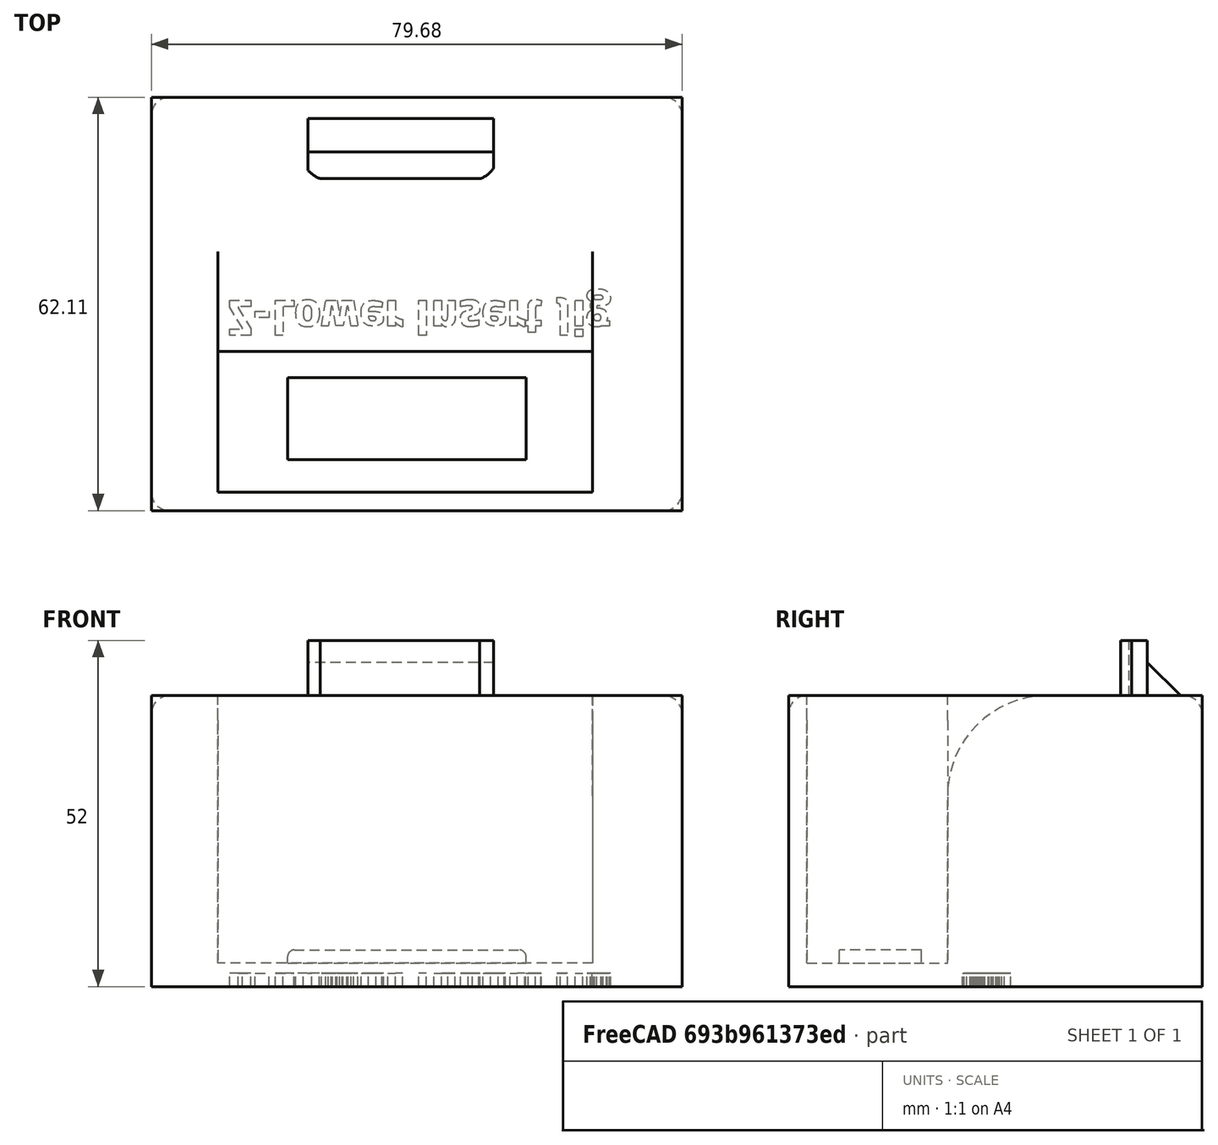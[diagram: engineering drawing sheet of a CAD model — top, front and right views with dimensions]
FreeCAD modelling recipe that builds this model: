
FCSTD DOCUMENT  (FreeCAD 0.17R9643 (Git))
Label: Z_lower_left_insert_jig
License: All rights reserved
LicenseURL: http://en.wikipedia.org/wiki/All_rights_reserved
objects: Sketcher::SketchObject×4, PartDesign::Pad×4, PartDesign::Fillet×3, PartDesign::Body×3, PartDesign::Pocket×2, PartDesign::Plane×2, Mesh::Feature×1, Part::Feature×1, PartDesign::Chamfer×1, Part::Part2DObjectPython×1, App::Part×1
note: 27 computed .brp shape members not serialized (recipe doc carries the construction recipe); baked Part::Feature solids carry a one-line shape summary decoded from their .brp

FEATURE [Sketcher::SketchObject] Sketch
  MapMode = 5
  Support = -> [XY_Plane002]
  sketch-geometry (4):
    g0: LineSegment StartX=-4.40933 StartY=-31.5823 StartZ=0 EndX=75.2715 EndY=-31.5823 EndZ=0
    g1: LineSegment StartX=75.2715 StartY=-31.5823 StartZ=0 EndX=75.2715 EndY=30.5279 EndZ=0
    g2: LineSegment StartX=75.2715 StartY=30.5279 StartZ=0 EndX=-4.40933 EndY=30.5279 EndZ=0
    g3: LineSegment StartX=-4.40933 StartY=30.5279 StartZ=0 EndX=-4.40933 EndY=-31.5823 EndZ=0
  constraints (8):
    c: Coincident(g0,g1)
    c: Coincident(g1,g2)
    c: Coincident(g2,g3)
    c: Coincident(g3,g0)
    c: Horizontal(g0)
    c: Horizontal(g2)
    c: Vertical(g1)
    c: Vertical(g3)
FEATURE [Mesh::Feature] z_lower_left_v2_5  label="z_lower_left_v2.5"
  Placement = pos=(0.517638,0,70.9319) rot=(0,1,0;1.5708rad)
FEATURE [PartDesign::Pad] Pad
  Length = 40
  Length2 = 100
  Profile = -> Sketch
  Type = 0
FEATURE [Sketcher::SketchObject] Sketch002
  MapMode = 5
  Placement = pos=(0,0,40) rot=(0,0,1;0rad)
  Support = -> [Pad]
  sketch-geometry (4):
    g0: LineSegment StartX=5.55641 StartY=-7.68423 StartZ=0 EndX=61.8518 EndY=-7.68423 EndZ=0
    g1: LineSegment StartX=61.8518 StartY=-7.68423 StartZ=0 EndX=61.8518 EndY=-28.8161 EndZ=0
    g2: LineSegment StartX=61.8518 StartY=-28.8161 StartZ=0 EndX=5.55641 EndY=-28.8161 EndZ=0
    g3: LineSegment StartX=5.55641 StartY=-28.8161 StartZ=0 EndX=5.55641 EndY=-7.68423 EndZ=0
  constraints (8):
    c: Coincident(g0,g1)
    c: Coincident(g1,g2)
    c: Horizontal(g0)
    c: Horizontal(g2)
    c: Vertical(g1)
    c: Vertical(g3)
    c: Coincident(g0,g3)
    c: Coincident(g2,g3)
FEATURE [PartDesign::Pocket] Pocket
  BaseFeature = -> Pad
  Length = 36.5
  Profile = -> Sketch002
  Type = 0
FEATURE [Part::Feature] Fillet002001  label="Fillet003"
  shape: bbox 79.68 x 62.11 x 52 mm, 25 faces (baked)
FEATURE [PartDesign::Fillet] Fillet
  Base = -> Fillet002001 [Edge31]
  BaseFeature = -> Fillet002001
  Radius = 15
FEATURE [PartDesign::Fillet] Fillet002002
  Base = -> Fillet [Edge47,Edge50,Edge25,Edge24,Edge23,Edge44,Edge22,Edge46]
  BaseFeature = -> Fillet
  Radius = 2.7
FEATURE [PartDesign::Chamfer] Chamfer
  Base = -> Fillet002002 [Edge16]
  BaseFeature = -> Fillet002002
  Size = 5
FEATURE [Part::Part2DObjectPython] ShapeString  # Draft 2D object (typed FeaturePython)
  FontFile = <userpath>/Desktop/Titillium-BoldUpright.otf
  Placement = pos=(7,0,0) rot=(1,0,0;3.14159rad)
  Size = 3
  String = Z-Lower Insert Jig
  Support = -> [Chamfer]
  Tracking = 70
FEATURE [PartDesign::Plane] DatumPlane
  MapMode = 5
  Placement = pos=(0,0,40) rot=(0,0,1;0rad)
  Support = -> [XY_Plane002]
  superPlacement = pos=(0,0,40) rot=(0,0,1;0rad)
FEATURE [Sketcher::SketchObject] Sketch003
  MapMode = 5
  Placement = pos=(0,0,40) rot=(0,0,1;0rad)
  Support = -> [DatumPlane]
  sketch-geometry (6):
    g0: LineSegment StartX=46.9902 StartY=22.3149 StartZ=0 EndX=19.1187 EndY=22.3149 EndZ=0
    g1: LineSegment StartX=19.1187 StartY=22.3149 StartZ=0 EndX=19.1187 EndY=19.5398 EndZ=0
    g2: LineSegment StartX=20.9285 StartY=18.2849 StartZ=0 EndX=44.8752 EndY=18.2849 EndZ=0
    g3: LineSegment StartX=46.9902 StartY=19.9178 StartZ=0 EndX=46.9902 EndY=22.3149 EndZ=0
    g4: ArcOfCircle CenterX=22.7284 CenterY=22.8131 CenterZ=0 NormalX=0 NormalY=0 NormalZ=1 Radius=4.87276 StartAngle=3.87815 EndAngle=4.33406
    g5: ArcOfCircle CenterX=43.9433 CenterY=21.6781 CenterZ=0 NormalX=0 NormalY=0 NormalZ=1 Radius=3.51879 StartAngle=4.98041 EndAngle=5.75929
  constraints (11):
    c: Coincident(g0,g1)
    c: Coincident(g3,g0)
    c: Horizontal(g0)
    c: Horizontal(g2)
    c: Vertical(g1)
    c: Vertical(g3)
    c: PointOnObject(g1,g4)
    c: Coincident(g2,g4)
    c: Coincident(g3,g5)
    c: Coincident(g2,g5)
    c: Coincident(g1,g4)
FEATURE [PartDesign::Pad] Pad001
  BaseFeature = -> Pocket
  Length = 12
  Length2 = 100
  Profile = -> Sketch003
  Type = 0
FEATURE [PartDesign::Pad] Pad002
  BaseFeature = -> Pad001
  Length = 3.7
  Length2 = 100
  Profile = -> Pad001 [Face5]
  Type = 0
FEATURE [PartDesign::Plane] DatumPlane001
  MapMode = 5
  Placement = pos=(0,0,3.5) rot=(0,0,1;0rad)
  Support = -> [XY_Plane002]
  superPlacement = pos=(0,0,3.5) rot=(0,0,1;0rad)
FEATURE [Sketcher::SketchObject] Sketch004
  MapMode = 5
  Placement = pos=(0,0,3.5) rot=(0,0,1;0rad)
  Support = -> [DatumPlane001]
  sketch-geometry (4):
    g0: LineSegment StartX=16.0405 StartY=-23.9483 StartZ=0 EndX=51.8657 EndY=-23.9483 EndZ=0
    g1: LineSegment StartX=51.8657 StartY=-23.9483 StartZ=0 EndX=51.8657 EndY=-11.6195 EndZ=0
    g2: LineSegment StartX=51.8657 StartY=-11.6195 StartZ=0 EndX=16.0405 EndY=-11.6195 EndZ=0
    g3: LineSegment StartX=16.0405 StartY=-11.6195 StartZ=0 EndX=16.0405 EndY=-23.9483 EndZ=0
  constraints (8):
    c: Coincident(g0,g1)
    c: Coincident(g1,g2)
    c: Coincident(g2,g3)
    c: Coincident(g3,g0)
    c: Horizontal(g0)
    c: Horizontal(g2)
    c: Vertical(g1)
    c: Vertical(g3)
FEATURE [PartDesign::Pad] Pad002002
  BaseFeature = -> Pad002
  Length = 2
  Length2 = 100
  Profile = -> Sketch004
  Type = 0
FEATURE [PartDesign::Fillet] Fillet002
  Base = -> Pad002002 [Edge70,Edge67]
  BaseFeature = -> Pad002002
  Radius = 1
FEATURE [PartDesign::Body] Fillet002Body
  Group = -> [Sketch,Pad,Sketch002,Pocket,DatumPlane,Sketch003,Pad001,Pad002,DatumPlane001,Sketch004,Pad002002,Fillet002]
  Origin = -> Fillet002BodyOrigin
  Tip = -> Fillet002
FEATURE [PartDesign::Body] ChamferBody
  BaseFeature = -> Fillet002001
  Group = -> [Fillet,Fillet002002,Chamfer]
  Origin = -> ChamferBodyOrigin
  Tip = -> Chamfer
FEATURE [App::Part] Part
  Group = -> [Fillet002Body,ChamferBody]
  License = CC BY 3.0
  LicenseURL = http://creativecommons.org/licenses/by/3.0/
  Origin = -> PartOrigin
FEATURE [PartDesign::Pocket] Pocket001
  Length = 2
  Profile = -> ShapeString
  Type = 0
FEATURE [PartDesign::Body] Body
  Group = -> [Pocket001]
  Origin = -> BodyOrigin
  Tip = -> Pocket001
